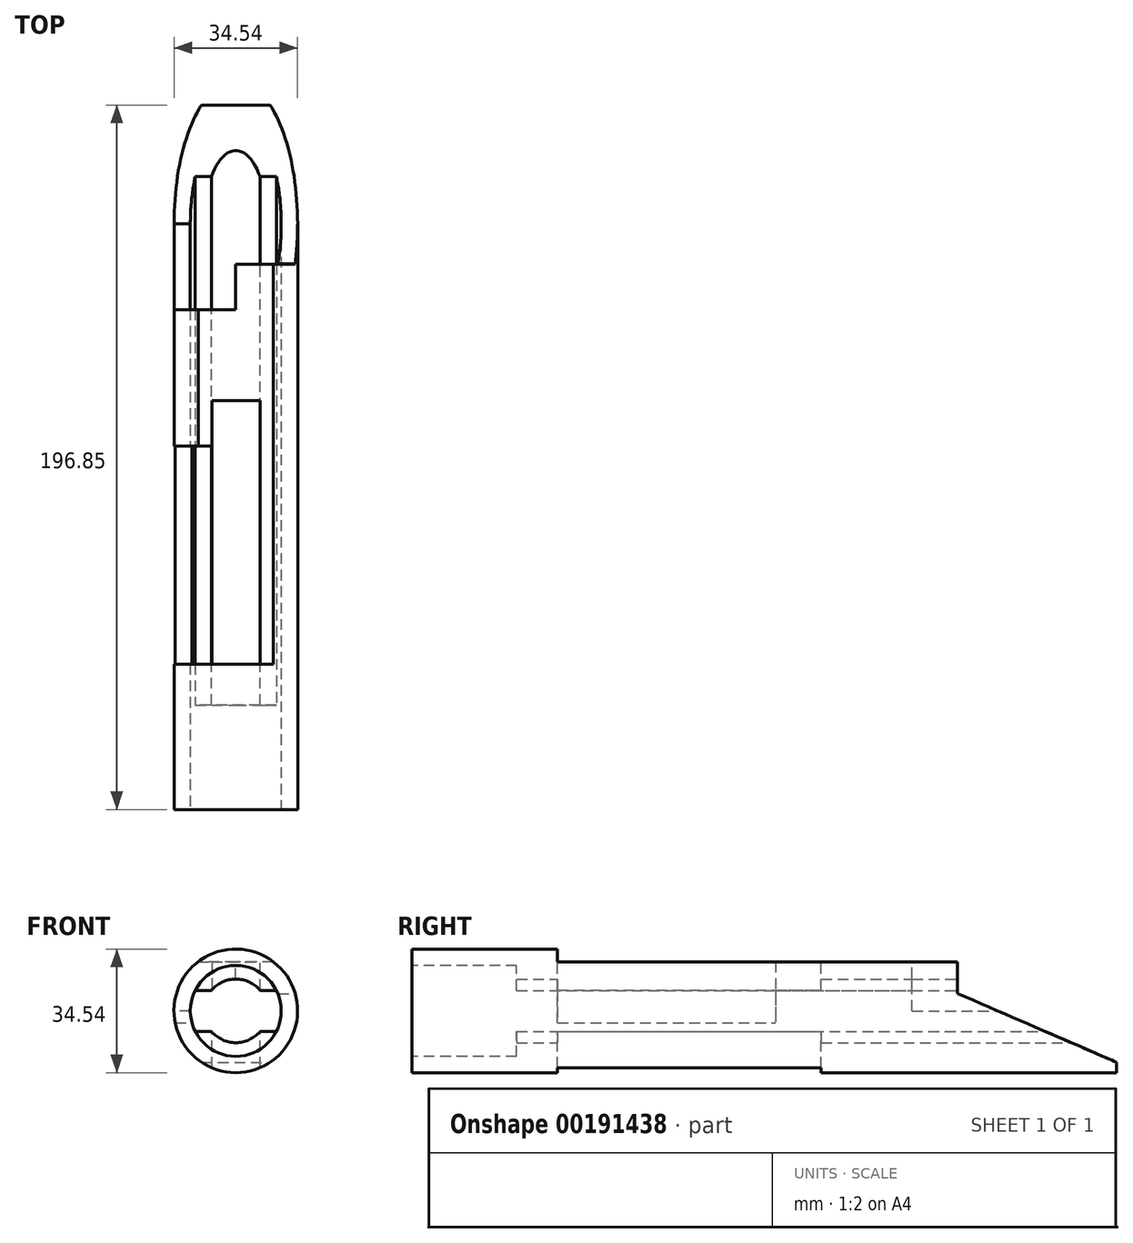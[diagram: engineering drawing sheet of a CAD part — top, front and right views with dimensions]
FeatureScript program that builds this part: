
annotation { "Feature Type Name" : "Feature", "Feature Type Description" : "" }
export const myFeature = defineFeature(function(context is Context, id is Id, definition is map)
    precondition{}
    {
        {
            var Q0;
            Q0=qCreatedBy(makeId("Front.planeOp"),FACE);
            var sketch = newSketch(context, id + "F0", { "sketchPlane" : qUnion([Q0])});
            skCircle(sketch, "E0", {"center": v(0, 0) * mm, "radius": 17.27 * mm});
            skCircle(sketch, "E1", {"center": v(0, 0) * mm, "radius": 8.89 * mm});
            skSolve(sketch);
        }
        {
            var Q0;
            Q0 = qSketchRegion(id + "F0", true);
            extrude(context, id + "F1", {"entities" : qUnion([Q0]), "depth" : 196.85 * mm});
        }
        {
            var Q0;
            Q0=makeQuery(id+"F1.opExtrude","CAP_FACE",FACE,{"disambiguationData":[OSD([sQuery(id+"F0.wireOp",EDGE,"E0"),sQuery(id+"F0.wireOp",EDGE,"E1")])],"isStart":false});
            var sketch = newSketch(context, id + "F2", { "sketchPlane" : qUnion([Q0])});
            skCircle(sketch, "E2", {"center": v(0, 0) * mm, "radius": 12.7 * mm});
            skSolve(sketch);
        }
        {
            var Q0;
            Q0 = qSketchRegion(id + "F2", true);
            extrude(context, id + "F3", {"entities" : qUnion([Q0]), "operationType" : NewBodyOperationType.REMOVE, "oppositeDirection" : true, "depth" : 29.2 * mm});
        }
        {
            var Q0;
            Q0=makeQuery(id+"F1.opExtrude","CAP_FACE",FACE,{"disambiguationData":[OSD([sQuery(id+"F0.wireOp",EDGE,"E0"),sQuery(id+"F0.wireOp",EDGE,"E1")])],"isStart":false});
            var sketch = newSketch(context, id + "F4", { "sketchPlane" : qUnion([Q0])});
            skArc(sketch, "E3", {"start": v(-11.34, 5.71) * mm, "mid": v(-12.7, 0) * mm, "end": v(-11.34, -5.71) * mm});
            skLineSegment(sketch, "E4", {"start": v(-11.34, 5.72) * mm, "end": v(11.34, 5.72) * mm});
            skLineSegment(sketch, "E5", {"start": v(-11.34, -5.72) * mm, "end": v(11.34, -5.72) * mm});
            skArc(sketch, "E6.trimOffspring", {"start": v(11.34, -5.71) * mm, "mid": v(12.7, 0) * mm, "end": v(11.34, 5.72) * mm});
            skSolve(sketch);
        }
        {
            var Q0;
            Q0 = qSketchRegion(id + "F4", true);
            extrude(context, id + "F5", {"entities" : qUnion([Q0]), "operationType" : NewBodyOperationType.REMOVE, "endBound" : BoundingType.THROUGH_ALL, "oppositeDirection" : true, "depth" : 25.4 * mm});
        }
        {
            var Q0;
            Q0=qCreatedBy(makeId("Right.planeOp"),FACE);
            var sketch = newSketch(context, id + "F6", { "sketchPlane" : qUnion([Q0])});
            skLineSegment(sketch, "E7.bottom", {"start": v(-156.21, 26.76) * mm, "end": v(57.64, 26.76) * mm});
            skLineSegment(sketch, "E7.top", {"start": v(-156.21, 13.72) * mm, "end": v(57.64, 13.72) * mm});
            skLineSegment(sketch, "E7.left", {"start": v(-156.21, 26.76) * mm, "end": v(-156.21, 13.72) * mm});
            skLineSegment(sketch, "E7.right", {"start": v(57.64, 26.76) * mm, "end": v(57.64, 13.72) * mm});
            skSolve(sketch);
        }
        {
            var Q0;
            Q0=makeQuery(id+"F6.imprint","IMPRINT",FACE,{"disambiguationData":[TD([[makeQuery(id+"F6.imprint","IMPRINT",EDGE,{"derivedFrom":sQuery(id+"F6.wireOp",EDGE,"E7.bottom")}),-1.0]])]});
            extrude(context, id + "F7", {"entities" : qUnion([Q0]), "operationType" : NewBodyOperationType.REMOVE, "endBound" : BoundingType.THROUGH_ALL, "depth" : 25.4 * mm, "hasSecondDirection" : true, "secondDirectionBound" : BoundingType.THROUGH_ALL, "secondDirectionOppositeDirection" : true, "secondDirectionDepth" : 25.4 * mm});
        }
        {
            var Q0;
            Q0=qCreatedBy(makeId("Right.planeOp"),FACE);
            var sketch = newSketch(context, id + "F8", { "sketchPlane" : qUnion([Q0])});
            skLineSegment(sketch, "E8.bottom", {"start": v(-57.15, 0) * mm, "end": v(7.94, 0) * mm});
            skLineSegment(sketch, "E8.top", {"start": v(-57.15, 18.94) * mm, "end": v(7.94, 18.94) * mm});
            skLineSegment(sketch, "E8.left", {"start": v(-57.15, 0) * mm, "end": v(-57.15, 18.94) * mm});
            skLineSegment(sketch, "E8.right", {"start": v(7.94, 0) * mm, "end": v(7.94, 18.94) * mm});
            skSolve(sketch);
        }
        {
            var Q0;
            Q0=makeQuery(id+"F8.imprint","IMPRINT",FACE,{"disambiguationData":[TD([[makeQuery(id+"F8.imprint","IMPRINT",EDGE,{"derivedFrom":sQuery(id+"F8.wireOp",EDGE,"E8.bottom")}),1.0]])]});
            extrude(context, id + "F9", {"entities" : qUnion([Q0]), "operationType" : NewBodyOperationType.REMOVE, "endBound" : BoundingType.THROUGH_ALL, "oppositeDirection" : true, "depth" : 25.4 * mm});
        }
        {
            var Q0;
            Q0=qCreatedBy(makeId("Right.planeOp"),FACE);
            var sketch = newSketch(context, id + "F10", { "sketchPlane" : qUnion([Q0])});
            skLineSegment(sketch, "E9.bottom", {"start": v(-44.45, 20.05) * mm, "end": v(14.07, 20.05) * mm});
            skLineSegment(sketch, "E9.top", {"start": v(-44.45, 4.83) * mm, "end": v(14.07, 4.83) * mm});
            skLineSegment(sketch, "E9.left", {"start": v(-44.45, 20.05) * mm, "end": v(-44.45, 4.83) * mm});
            skLineSegment(sketch, "E9.right", {"start": v(14.07, 20.05) * mm, "end": v(14.07, 4.83) * mm});
            skSolve(sketch);
        }
        {
            var Q0;
            Q0=makeQuery(id+"F10.imprint","IMPRINT",FACE,{"disambiguationData":[TD([[makeQuery(id+"F10.imprint","IMPRINT",EDGE,{"derivedFrom":sQuery(id+"F10.wireOp",EDGE,"E9.bottom")}),-1.0]])]});
            extrude(context, id + "F11", {"entities" : qUnion([Q0]), "operationType" : NewBodyOperationType.REMOVE, "endBound" : BoundingType.THROUGH_ALL, "depth" : 25.4 * mm});
        }
        {
            var Q0;
            Q0=qCreatedBy(makeId("Right.planeOp"),FACE);
            var sketch = newSketch(context, id + "F12", { "sketchPlane" : qUnion([Q0])});
            skLineSegment(sketch, "E10", {"start": v(-44.4, 4.81) * mm, "end": v(8.06, -17.87) * mm});
            skLineSegment(sketch, "E11", {"start": v(8.06, -17.87) * mm, "end": v(8.06, 8.4) * mm});
            skLineSegment(sketch, "E12", {"start": v(8.06, 8.4) * mm, "end": v(-43.8, 8.4) * mm});
            skLineSegment(sketch, "E13", {"start": v(-43.8, 8.4) * mm, "end": v(-44.4, 4.8) * mm});
            skSolve(sketch);
        }
        {
            var Q0;
            Q0 = qSketchRegion(id + "F12", true);
            extrude(context, id + "F13", {"entities" : qUnion([Q0]), "operationType" : NewBodyOperationType.REMOVE, "endBound" : BoundingType.THROUGH_ALL, "oppositeDirection" : true, "depth" : 25.4 * mm, "hasSecondDirection" : true, "secondDirectionBound" : BoundingType.THROUGH_ALL, "secondDirectionOppositeDirection" : false, "secondDirectionDepth" : 25.4 * mm});
        }
        {
            var Q0;
            Q0=qCreatedBy(makeId("Top.planeOp"),FACE);
            var sketch = newSketch(context, id + "F14", { "sketchPlane" : qUnion([Q0])});
            skLineSegment(sketch, "E14.bottom", {"start": v(-6.73, -156.21) * mm, "end": v(6.73, -156.21) * mm});
            skLineSegment(sketch, "E14.top", {"start": v(-6.73, -82.55) * mm, "end": v(6.73, -82.55) * mm});
            skLineSegment(sketch, "E14.left", {"start": v(-6.73, -156.21) * mm, "end": v(-6.73, -82.55) * mm});
            skLineSegment(sketch, "E14.right", {"start": v(6.73, -156.21) * mm, "end": v(6.73, -82.55) * mm});
            skPoint(sketch, "E14.middle", {"position": v(0, -119.38) * mm});
            skSolve(sketch);
        }
        {
            var Q0;
            Q0 = qSketchRegion(id + "F14", true);
            extrude(context, id + "F15", {"entities" : qUnion([Q0]), "operationType" : NewBodyOperationType.REMOVE, "endBound" : BoundingType.THROUGH_ALL, "oppositeDirection" : true, "depth" : 25.4 * mm, "hasSecondDirection" : true, "secondDirectionBound" : BoundingType.THROUGH_ALL, "secondDirectionOppositeDirection" : false, "secondDirectionDepth" : 25.4 * mm});
        }
        {
            var Q0;
            Q0=qCreatedBy(makeId("Right.planeOp"),FACE);
            var sketch = newSketch(context, id + "F16", { "sketchPlane" : qUnion([Q0])});
            skLineSegment(sketch, "E15.bottom", {"start": v(-156.21, 18.6) * mm, "end": v(-95.25, 18.6) * mm});
            skLineSegment(sketch, "E15.top", {"start": v(-156.21, -3.34) * mm, "end": v(-95.25, -3.34) * mm});
            skLineSegment(sketch, "E15.left", {"start": v(-156.21, 18.6) * mm, "end": v(-156.21, -3.34) * mm});
            skLineSegment(sketch, "E15.right", {"start": v(-95.25, 18.6) * mm, "end": v(-95.25, -3.34) * mm});
            skSolve(sketch);
        }
        {
            var Q0;
            Q0 = qSketchRegion(id + "F16", true);
            extrude(context, id + "F17", {"entities" : qUnion([Q0]), "operationType" : NewBodyOperationType.REMOVE, "endBound" : BoundingType.THROUGH_ALL, "oppositeDirection" : true, "depth" : 25.4 * mm});
        }
    });
